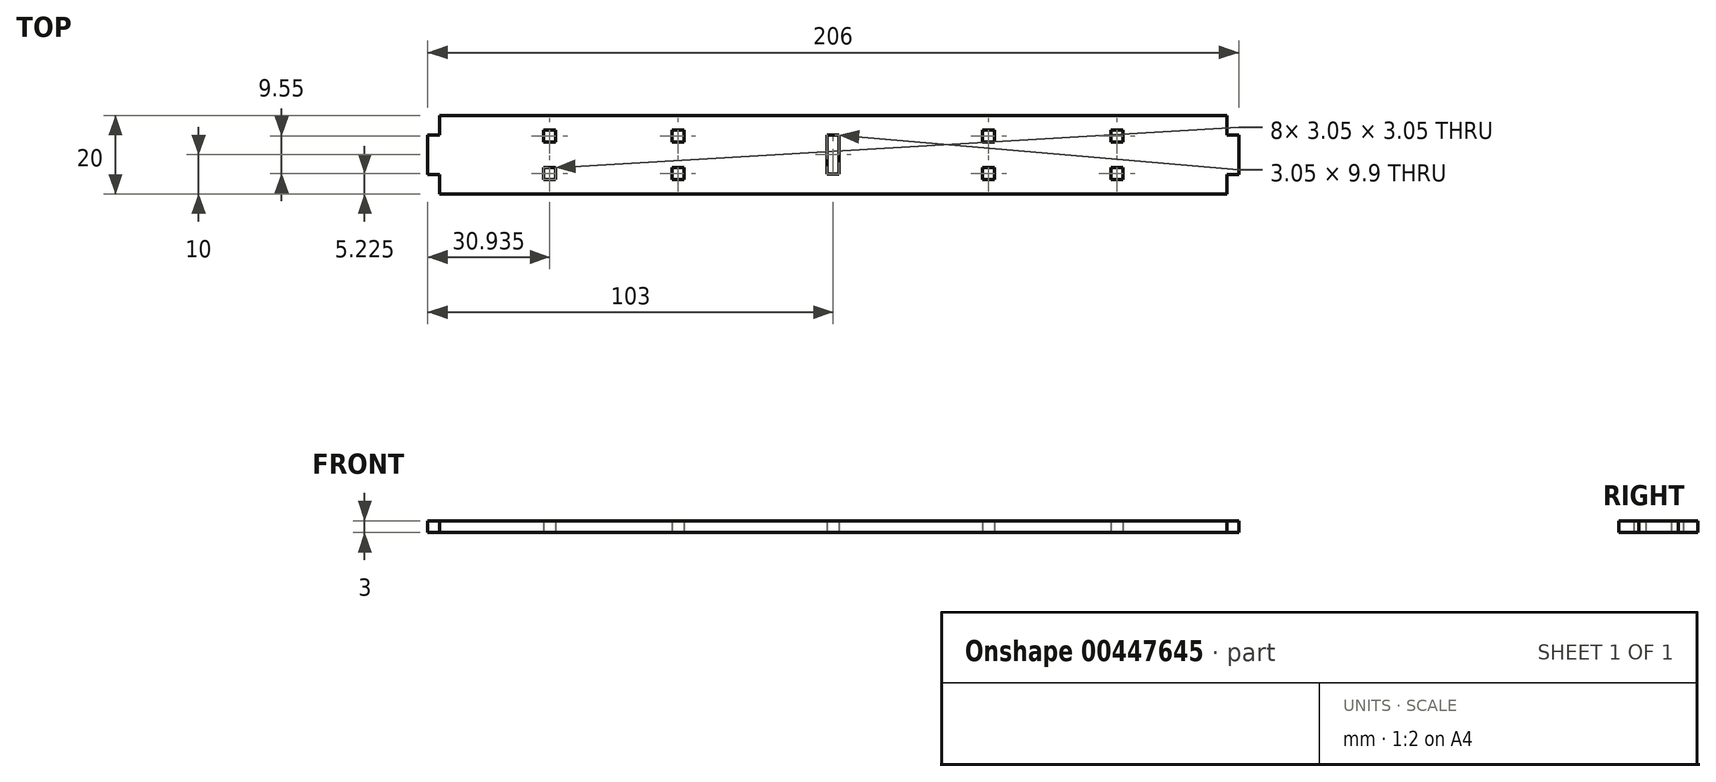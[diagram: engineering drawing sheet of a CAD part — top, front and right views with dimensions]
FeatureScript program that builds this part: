
annotation { "Feature Type Name" : "Feature", "Feature Type Description" : "" }
export const myFeature = defineFeature(function(context is Context, id is Id, definition is map)
    precondition{}
    {
        {
            var Q0;
            Q0=qCreatedBy(makeId("Top.planeOp"),FACE);
            var sketch = newSketch(context, id + "F0", { "sketchPlane" : qUnion([Q0])});
            skLineSegment(sketch, "E0.bottom", {"start": v(-100, -10) * mm, "end": v(100, -10) * mm});
            skLineSegment(sketch, "E0.top", {"start": v(-100, 10) * mm, "end": v(100, 10) * mm});
            skLineSegment(sketch, "E0.left", {"start": v(-100, -10) * mm, "end": v(-100, 10) * mm});
            skLineSegment(sketch, "E0.right", {"start": v(100, -10) * mm, "end": v(100, 10) * mm});
            skPoint(sketch, "E0.middle", {"position": v(0, 0) * mm});
            skLineSegment(sketch, "E1.bottom", {"start": v(-100, -5) * mm, "end": v(-103, -5) * mm});
            skLineSegment(sketch, "E1.top", {"start": v(-100, 5) * mm, "end": v(-103, 5) * mm});
            skLineSegment(sketch, "E1.left", {"start": v(-100, -5) * mm, "end": v(-100, 5) * mm});
            skLineSegment(sketch, "E1.right", {"start": v(-103, -5) * mm, "end": v(-103, 5) * mm});
            skPoint(sketch, "E1.middle", {"position": v(-101.5, 0) * mm});
            skLineSegment(sketch, "E2.bottom", {"start": v(103, -5) * mm, "end": v(100, -5) * mm});
            skLineSegment(sketch, "E2.top", {"start": v(103, 5) * mm, "end": v(100, 5) * mm});
            skLineSegment(sketch, "E2.left", {"start": v(103, -5) * mm, "end": v(103, 5) * mm});
            skLineSegment(sketch, "E2.right", {"start": v(100, -5) * mm, "end": v(100, 5) * mm});
            skPoint(sketch, "E2.middle", {"position": v(101.5, 0) * mm});
            skLineSegment(sketch, "E3.bottom", {"start": v(1.52, -4.95) * mm, "end": v(-1.53, -4.95) * mm});
            skLineSegment(sketch, "E3.top", {"start": v(1.52, 4.95) * mm, "end": v(-1.53, 4.95) * mm});
            skLineSegment(sketch, "E3.left", {"start": v(1.53, -4.95) * mm, "end": v(1.53, 4.95) * mm});
            skLineSegment(sketch, "E3.right", {"start": v(-1.52, -4.95) * mm, "end": v(-1.52, 4.95) * mm});
            skPoint(sketch, "E4.middle.positionSnap0", {"position": v(0, -10) * mm});
            skPoint(sketch, "E4.centerSnap0", {"position": v(0, -10) * mm});
            skLineSegment(sketch, "E5.bottom", {"start": v(-70.54, 6.3) * mm, "end": v(-73.6, 6.3) * mm});
            skLineSegment(sketch, "E5.top", {"start": v(-70.54, 3.25) * mm, "end": v(-73.6, 3.25) * mm});
            skLineSegment(sketch, "E5.left", {"start": v(-70.54, 6.3) * mm, "end": v(-70.54, 3.25) * mm});
            skLineSegment(sketch, "E5.right", {"start": v(-73.6, 6.3) * mm, "end": v(-73.6, 3.25) * mm});
            skPoint(sketch, "E5.middle", {"position": v(-72.06, 4.77) * mm});
            skLineSegment(sketch, "E6.bottom", {"start": v(-70.54, -6.3) * mm, "end": v(-73.6, -6.3) * mm});
            skLineSegment(sketch, "E6.top", {"start": v(-70.54, -3.25) * mm, "end": v(-73.6, -3.25) * mm});
            skLineSegment(sketch, "E6.left", {"start": v(-70.54, -6.3) * mm, "end": v(-70.54, -3.25) * mm});
            skLineSegment(sketch, "E6.right", {"start": v(-73.6, -6.3) * mm, "end": v(-73.6, -3.25) * mm});
            skPoint(sketch, "E6.middle", {"position": v(-72.06, -4.78) * mm});
            skLineSegment(sketch, "E7.bottom", {"start": v(-37.94, 3.25) * mm, "end": v(-40.99, 3.25) * mm});
            skLineSegment(sketch, "E7.top", {"start": v(-37.94, 6.3) * mm, "end": v(-40.99, 6.3) * mm});
            skLineSegment(sketch, "E7.left", {"start": v(-37.94, 3.25) * mm, "end": v(-37.94, 6.3) * mm});
            skLineSegment(sketch, "E7.right", {"start": v(-40.99, 3.25) * mm, "end": v(-40.99, 6.3) * mm});
            skPoint(sketch, "E7.middle", {"position": v(-39.46, 4.78) * mm});
            skLineSegment(sketch, "E8.bottom", {"start": v(-37.94, -6.3) * mm, "end": v(-40.99, -6.3) * mm});
            skLineSegment(sketch, "E8.top", {"start": v(-37.94, -3.25) * mm, "end": v(-40.98, -3.25) * mm});
            skLineSegment(sketch, "E8.left", {"start": v(-37.94, -6.3) * mm, "end": v(-37.94, -3.25) * mm});
            skLineSegment(sketch, "E8.right", {"start": v(-40.98, -6.3) * mm, "end": v(-40.98, -3.25) * mm});
            skPoint(sketch, "E8.middle", {"position": v(-39.46, -4.78) * mm});
            skLineSegment(sketch, "E9.bottom", {"start": v(73.6, -6.3) * mm, "end": v(70.54, -6.3) * mm});
            skLineSegment(sketch, "E9.top", {"start": v(73.6, -3.25) * mm, "end": v(70.54, -3.25) * mm});
            skLineSegment(sketch, "E9.left", {"start": v(73.6, -6.3) * mm, "end": v(73.6, -3.25) * mm});
            skLineSegment(sketch, "E9.right", {"start": v(70.54, -6.3) * mm, "end": v(70.54, -3.25) * mm});
            skPoint(sketch, "E9.middle", {"position": v(72.06, -4.78) * mm});
            skLineSegment(sketch, "E10.bottom", {"start": v(73.6, 3.25) * mm, "end": v(70.54, 3.25) * mm});
            skLineSegment(sketch, "E10.top", {"start": v(73.6, 6.3) * mm, "end": v(70.54, 6.3) * mm});
            skLineSegment(sketch, "E10.left", {"start": v(73.6, 3.25) * mm, "end": v(73.6, 6.3) * mm});
            skLineSegment(sketch, "E10.right", {"start": v(70.54, 3.25) * mm, "end": v(70.54, 6.3) * mm});
            skPoint(sketch, "E10.middle", {"position": v(72.06, 4.77) * mm});
            skPoint(sketch, "E10.middle.positionSnap0", {"position": v(72.06, -3.25) * mm});
            skPoint(sketch, "E10.centerSnap0", {"position": v(72.06, -3.25) * mm});
            skLineSegment(sketch, "E11.bottom", {"start": v(40.98, 3.25) * mm, "end": v(37.93, 3.25) * mm});
            skLineSegment(sketch, "E11.top", {"start": v(40.98, 6.3) * mm, "end": v(37.93, 6.3) * mm});
            skLineSegment(sketch, "E11.left", {"start": v(40.98, 3.25) * mm, "end": v(40.98, 6.3) * mm});
            skLineSegment(sketch, "E11.right", {"start": v(37.93, 3.25) * mm, "end": v(37.93, 6.3) * mm});
            skPoint(sketch, "E11.middle", {"position": v(39.46, 4.77) * mm});
            skLineSegment(sketch, "E12.bottom", {"start": v(40.98, -6.3) * mm, "end": v(37.93, -6.3) * mm});
            skLineSegment(sketch, "E12.top", {"start": v(40.98, -3.25) * mm, "end": v(37.93, -3.25) * mm});
            skLineSegment(sketch, "E12.left", {"start": v(40.98, -6.3) * mm, "end": v(40.98, -3.25) * mm});
            skLineSegment(sketch, "E12.right", {"start": v(37.93, -6.3) * mm, "end": v(37.93, -3.25) * mm});
            skPoint(sketch, "E12.middle", {"position": v(39.46, -4.78) * mm});
            skPoint(sketch, "E12.middle.positionSnap0", {"position": v(39.46, 3.25) * mm});
            skPoint(sketch, "E12.centerSnap0", {"position": v(39.46, 3.25) * mm});
            skSolve(sketch);
        }
        {
            var Q0;
            Q0 = qSketchRegion(id + "F0", true);
            extrude(context, id + "F1", {"entities" : qUnion([Q0]), "depth" : 3 * mm});
        }
    });
